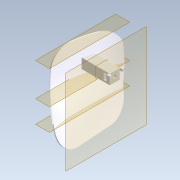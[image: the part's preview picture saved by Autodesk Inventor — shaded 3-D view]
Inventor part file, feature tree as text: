
AUTODESK INVENTOR PART (.ipt)
format: ipt  version: 2020.2 (Build 242310000, 310)  size: 370,688 bytes
history: native  units: mm
features: sketch x9, plane x5, extrude x5, loft x1, fillet x1
ambient origin geometry x8: Origin, YZ Plane, XZ Plane, XY Plane, X Axis, Y Axis, Z Axis, Center Point
bodies: Solid1 (feature_tree)
feature tree (21):
  sketch  "Sketch1"  dims[d0=1.0mm d1=20.0mm d2=1.0mm]
  plane  "Work Plane1"
  sketch  "Sketch2"  dims[d3=20.0mm d4=1.0mm]
  plane  "Work Plane2"
  sketch  "Sketch3"  dims[d5=30.0mm d6=1.0mm]
  plane  "Work Plane3"
  loft  "Loft1"
  fillet  "Fillet1"  Radius=1.0mm
  plane  "Work Plane4"
  extrude  "Extrusion1"  Depth=1.0mm
  extrude  "Extrusion2"  Depth=1.0mm
  extrude  "Extrusion3"  TaperAngle=0.0deg  [1 undecoded]
  extrude  "Extrusion4"  Depth=10.0mm TaperAngle=90.0deg
  plane  "Work Plane6"
  extrude  "Extrusion5"  Depth=15.0mm
  sketch  "Sketch4"  dims[d7=0.0mm d8=90.0deg d9=0.0mm d10=90.0deg]
  sketch  "Sketch5"  dims[d11=0.0mm d12=90.0deg d13=10.0mm d14=90.0deg]
  sketch  "Sketch6"  dims[d15=15.0mm d16=15.0mm]
  sketch  "Sketch7"  dims[d17=9.0mm]
  sketch  "Sketch8"  dims[d18=9.0mm]
  sketch  "Sketch9"  dims[d19=3.0mm d20=0.0mm d21=0.0mm d23=3.0mm d24=3.0mm d25=2.5mm d26=6.0mm d27=10.0mm d28=0.0mm d29=0.2mm d30=2.0mm d31=2.0mm d32=3.0mm d33=0.2mm d34=2.0mm d35=2.0mm d36=3.0mm d37=2.0mm d38=0.0mm d39=3.0mm d40=2.0mm d41=0.0mm d42=-12.0mm d43=6.0mm d44=10.0mm d45=0.0mm]
note: 1 required parameter value undecoded (feature->parameter linkage not recoverable at this tier; creation-order binding heuristic only, values carry confidence <= 0.55)
